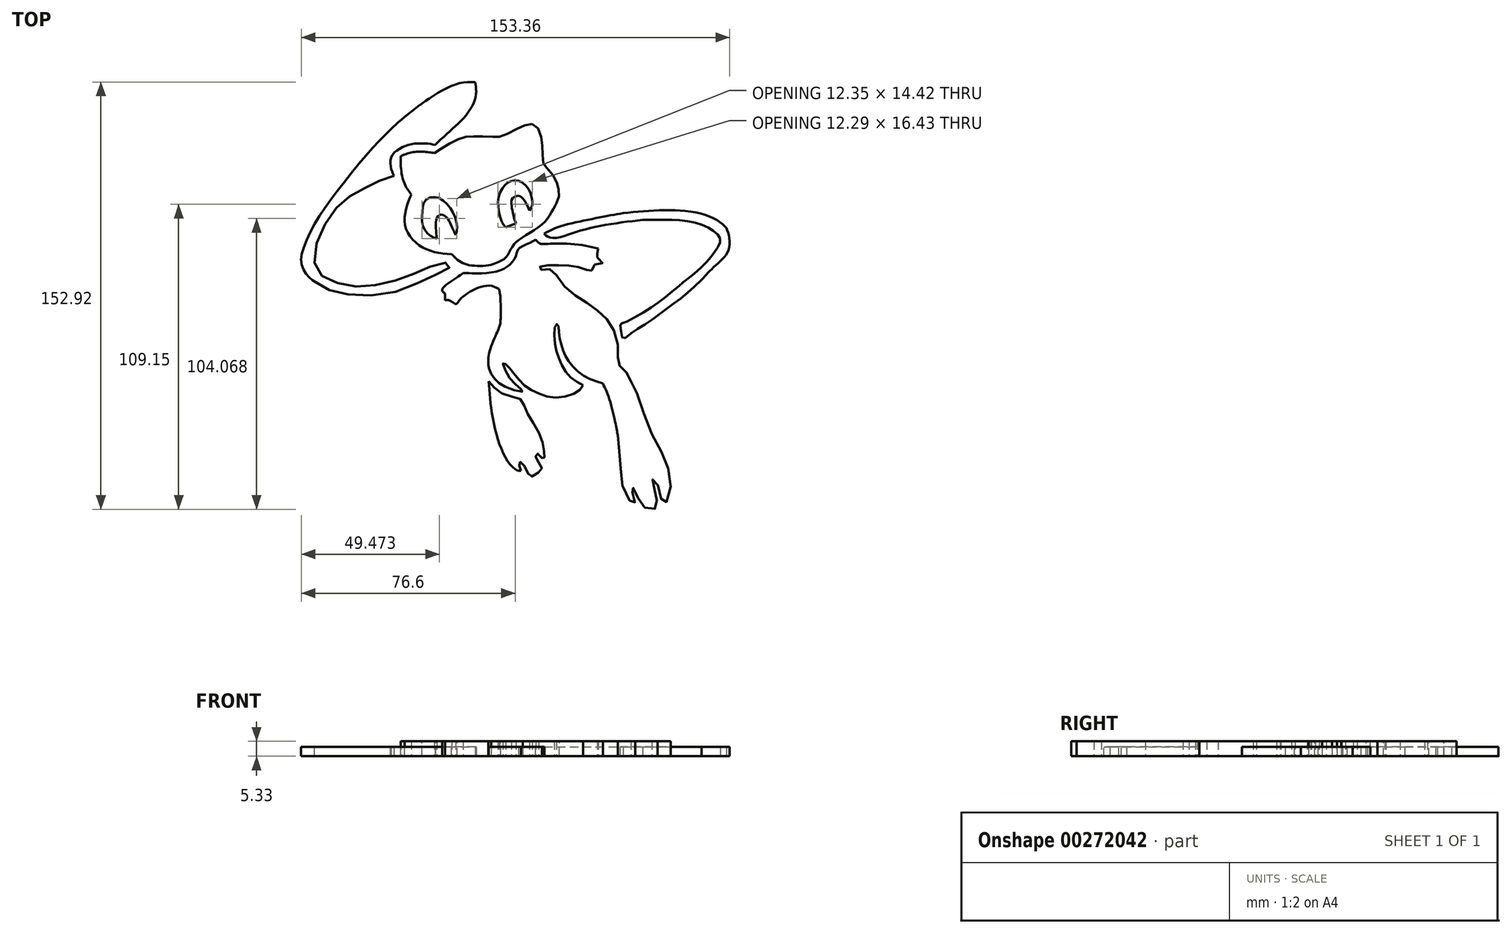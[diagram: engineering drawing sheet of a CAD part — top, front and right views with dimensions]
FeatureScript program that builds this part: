
annotation { "Feature Type Name" : "Feature", "Feature Type Description" : "" }
export const myFeature = defineFeature(function(context is Context, id is Id, definition is map)
    precondition{}
    {
        {
            var Q0;
            Q0=qCreatedBy(makeId("Top.planeOp"),FACE);
            var sketch = newSketch(context, id + "F0", { "sketchPlane" : qUnion([Q0])});
            skFitSpline(sketch, "E0", {"points": [v(-36.88, 36.08) * mm, v(-38.4, 38.25) * mm, v(-40.15, 42.6) * mm, v(-40.65, 48.33) * mm, v(-40.58, 49.85) * mm], "startDerivative": vector(-6.94, 9.09) * mm, "endDerivative": vector(0.6, 7.48) * mm});
            skFitSpline(sketch, "E1", {"points": [v(-40.58, 49.85) * mm, v(-38.04, 50.8) * mm, v(-34.93, 51.37) * mm, v(-31.38, 51.3) * mm, v(-28.55, 50.87) * mm], "startDerivative": vector(10.5, 4.31) * mm, "endDerivative": vector(11.28, -2.04) * mm});
            skFitSpline(sketch, "E2", {"points": [v(-28.55, 50.87) * mm, v(-24.87, 53.3) * mm, v(-19.99, 55.88) * mm, v(-16.36, 56.8) * mm, v(-12.2, 56.87) * mm, v(-6.98, 56.74) * mm, v(-4.41, 57) * mm, v(1, 59.57) * mm, v(4.83, 61.1) * mm, v(7.67, 60.76) * mm, v(9.65, 56.27) * mm, v(10.11, 52.11) * mm, v(10.44, 47.3) * mm, v(11.57, 45.71) * mm, v(14.54, 41.82) * mm, v(15.6, 38.91) * mm, v(16.05, 35.8) * mm, v(15.13, 32.97) * mm], "startDerivative": vector(55.8, 38.5) * mm, "endDerivative": vector(-24.9, -54.1) * mm});
            skFitSpline(sketch, "E3", {"points": [v(15.13, 32.97) * mm, v(13.23, 29.5) * mm, v(9.9, 25.32) * mm, v(3.54, 21.13) * mm, v(0, 18.38) * mm, v(-1.7, 15.62) * mm, v(-3.4, 13.15) * mm, v(-5.2, 12.2) * mm], "startDerivative": vector(-12.69, -24.26) * mm, "endDerivative": vector(-18.67, -6.95) * mm});
            skFitSpline(sketch, "E4", {"points": [v(-5.2, 12.2) * mm, v(-8.38, 10.92) * mm, v(-15.27, 10.68) * mm, v(-19.62, 12.2) * mm, v(-22.36, 14.64) * mm], "startDerivative": vector(-12.64, -6.7) * mm, "endDerivative": vector(-11.41, 11.76) * mm});
            skFitSpline(sketch, "E5", {"points": [v(-22.36, 14.64) * mm, v(-29.1, 15.62) * mm, v(-34.66, 18.38) * mm, v(-38.53, 23.3) * mm, v(-39.1, 28.91) * mm, v(-37.75, 33.9) * mm, v(-36.88, 36.08) * mm], "startDerivative": vector(-36.55, 3.17) * mm, "endDerivative": vector(7.3, 17.53) * mm});
            skFitSpline(sketch, "E6", {"points": [v(-27.74, 20.26) * mm, v(-28, 23.55) * mm, v(-27.97, 26.8) * mm, v(-27.14, 28.47) * mm, v(-25.9, 28.88) * mm, v(-24.15, 27.82) * mm, v(-22.83, 25.7) * mm, v(-21.65, 22.95) * mm, v(-20.94, 21.55) * mm], "startDerivative": vector(-1.85, 21.58) * mm, "endDerivative": vector(6.7, -12.08) * mm});
            skFitSpline(sketch, "E7", {"points": [v(-20.94, 21.55) * mm, v(-20.44, 24.42) * mm, v(-21.43, 28.58) * mm, v(-23.73, 32.29) * mm, v(-27.18, 34.9) * mm, v(-30.4, 34.9) * mm, v(-32.4, 32.97) * mm, v(-32.96, 29.53) * mm, v(-32.93, 25.74) * mm, v(-31.6, 22.72) * mm, v(-29.48, 20.98) * mm, v(-27.74, 20.26) * mm], "startDerivative": vector(8.86, 31.93) * mm, "endDerivative": vector(24.92, -8.61) * mm});
            skLineSegment(sketch, "E8", {"start": v(0.64, 25.77) * mm, "end": v(-3.1, 24.33) * mm});
            skFitSpline(sketch, "E9", {"points": [v(-3.1, 24.33) * mm, v(-4.7, 26.86) * mm, v(-5.73, 31.34) * mm, v(-5.33, 36.17) * mm, v(-3.1, 39.67) * mm, v(-0.97, 40.88) * mm, v(1.96, 40.82) * mm, v(4.95, 38.23) * mm, v(6.27, 34.79) * mm, v(6.39, 32.09) * mm, v(5.4, 30.37) * mm], "startDerivative": vector(-18.53, 24.2) * mm, "endDerivative": vector(-15.72, -20.8) * mm});
            skFitSpline(sketch, "E10", {"points": [v(5.4, 30.37) * mm, v(4.03, 33.3) * mm, v(2.36, 35.3) * mm, v(1.16, 35.6) * mm, v(-0.68, 34.67) * mm, v(-1.02, 32.66) * mm, v(-0.68, 30.37) * mm, v(0, 27.55) * mm, v(0.64, 25.77) * mm], "startDerivative": vector(-8.23, 19.96) * mm, "endDerivative": vector(5.68, -14.34) * mm});
            skFitSpline(sketch, "E11", {"points": [v(-28.3, 53.85) * mm, v(-22.62, 59.17) * mm, v(-17.41, 64.25) * mm, v(-14.15, 69.88) * mm, v(-13.66, 73.45) * mm, v(-13.97, 76.31) * mm], "startDerivative": vector(23.72, 22.62) * mm, "endDerivative": vector(-2.81, 19.35) * mm});
            skFitSpline(sketch, "E12", {"points": [v(-13.97, 76.31) * mm, v(-19.11, 76) * mm, v(-25.25, 73.58) * mm, v(-32.16, 69.26) * mm, v(-37.13, 65.53) * mm, v(-41.53, 61.88) * mm, v(-44.08, 59.5) * mm], "startDerivative": vector(-32.41, 0.3) * mm, "endDerivative": vector(-18.17, -17.44) * mm});
            skFitSpline(sketch, "E13", {"points": [v(-44.08, 59.5) * mm, v(-51.8, 51.48) * mm, v(-63.2, 37.48) * mm, v(-71.34, 25.77) * mm, v(-75.54, 16.64) * mm, v(-76.22, 11.77) * mm, v(-74.95, 8.38) * mm, v(-73.1, 6.15) * mm, v(-70.98, 4.61) * mm], "startDerivative": vector(-48.4, -47.85) * mm, "endDerivative": vector(29.7, -19.4) * mm});
            skFitSpline(sketch, "E14", {"points": [v(-70.98, 4.61) * mm, v(-65.73, 1.76) * mm, v(-56.11, 0) * mm, v(-41.53, 1.5) * mm, v(-30.47, 6.38) * mm, v(-23.8, 9.45) * mm, v(-22.65, 11) * mm, v(-25.86, 11.63) * mm, v(-32.16, 9.32) * mm, v(-40.09, 6.12) * mm, v(-50.09, 3.56) * mm, v(-58.94, 3.43) * mm, v(-66.88, 5.86) * mm, v(-70.98, 9.58) * mm, v(-70.98, 17.91) * mm, v(-66.24, 27.79) * mm, v(-60.86, 34.07) * mm, v(-54.7, 37.79) * mm, v(-48.55, 40.86) * mm, v(-43.04, 42.79) * mm], "startDerivative": vector(103.96, -66.84) * mm, "endDerivative": vector(119.1, 36.89) * mm});
            skFitSpline(sketch, "E15", {"points": [v(-43.04, 42.79) * mm, v(-44.08, 45.32) * mm, v(-44.08, 49.34) * mm, v(-41, 52.5) * mm, v(-36.55, 54.15) * mm, v(-31.3, 54.3) * mm, v(-28.3, 53.85) * mm], "startDerivative": vector(-8.33, 16.7) * mm, "endDerivative": vector(18.9, -3.53) * mm});
            skFitSpline(sketch, "E16", {"points": [v(7.73, 19.96) * mm, v(4.7, 18.38) * mm, v(1.47, 16.59) * mm, v(0.64, 14.22) * mm, v(-1.21, 11.37) * mm, v(-4.34, 9.18) * mm, v(-10.33, 7.93) * mm, v(-15.9, 7.9) * mm, v(-18.3, 8) * mm], "startDerivative": vector(-23.75, -13.65) * mm, "endDerivative": vector(-21.58, 1.02) * mm});
            skFitSpline(sketch, "E17", {"points": [v(-18.3, 8) * mm, v(-21.48, 5.79) * mm, v(-25.73, 2.22) * mm, v(-25.51, 1.24) * mm, v(-24.96, 0.69) * mm, v(-24.75, -0.76) * mm, v(-24.75, -1.78) * mm], "startDerivative": vector(-11.77, -8.3) * mm, "endDerivative": vector(-0.07, -7.72) * mm});
            skFitSpline(sketch, "E18", {"points": [v(-24.75, -1.78) * mm, v(-23.18, -1.78) * mm, v(-20.94, -3.12) * mm, v(-19.7, -1.78) * mm, v(-15.31, 1.57) * mm, v(-11.82, 3.08) * mm, v(-8.28, 3.4) * mm, v(-5.41, 2.2) * mm], "startDerivative": vector(14.29, 3.8) * mm, "endDerivative": vector(18.83, -10.57) * mm});
            skFitSpline(sketch, "E19", {"points": [v(-5.41, -11.46) * mm, v(-6.46, -13.9) * mm, v(-8.5, -18.88) * mm, v(-9.27, -22.77) * mm, v(-9.19, -25.46) * mm, v(-8.23, -28.1) * mm], "startDerivative": vector(-5.21, -12.45) * mm, "endDerivative": vector(6.45, -14.59) * mm});
            skFitSpline(sketch, "E20", {"points": [v(-5.41, -11.46) * mm, v(-5.02, -10.14) * mm, v(-4.86, -5.9) * mm, v(-5.02, -0.37) * mm, v(-5.41, 2.2) * mm], "startDerivative": vector(2.76, 6.94) * mm, "endDerivative": vector(-2.02, 10.26) * mm});
            skFitSpline(sketch, "E21", {"points": [v(-8.23, -28.1) * mm, v(-6.3, -30.62) * mm, v(-2.7, -32.95) * mm, v(3.02, -34.4) * mm, v(1.33, -32.7) * mm, v(-2.6, -28.1) * mm, v(-3.98, -24.1) * mm, v(-2.53, -25.15) * mm, v(0, -28.1) * mm, v(3.82, -32.39) * mm, v(9.45, -35.44) * mm, v(15.89, -36.57) * mm, v(22.56, -34.56) * mm, v(24.65, -32.14) * mm], "startDerivative": vector(28.07, -40.83) * mm, "endDerivative": vector(24.08, 39.06) * mm});
            skFitSpline(sketch, "E22", {"points": [v(24.65, -32.14) * mm, v(19.46, -28.61) * mm, v(16.04, -22.68) * mm, v(14.52, -16.3) * mm, v(14.9, -10.44) * mm, v(15.66, -10.59) * mm, v(15.96, -13.48) * mm, v(17.1, -18.5) * mm, v(18.55, -22.07) * mm, v(21.74, -26.25) * mm, v(26.3, -29.6) * mm, v(31.7, -31.5) * mm], "startDerivative": vector(-53.5, 28.4) * mm, "endDerivative": vector(55.72, -15.9) * mm});
            skFitSpline(sketch, "E23", {"points": [v(31.7, -31.5) * mm, v(33.83, -36.52) * mm, v(35.88, -44.2) * mm, v(36.72, -48.3) * mm, v(37.03, -50.06) * mm], "startDerivative": vector(8, -16.8) * mm, "endDerivative": vector(1.73, -10.31) * mm});
            skFitSpline(sketch, "E24", {"points": [v(37.03, -50.06) * mm, v(37.67, -56.88) * mm, v(38.28, -65.1) * mm, v(40.12, -71.84) * mm, v(43.18, -74.9) * mm, v(43.1, -73.5) * mm, v(42.4, -70.97) * mm, v(41.78, -68.6) * mm, v(42.74, -69.04) * mm, v(44.05, -72.02) * mm, v(46.24, -75.6) * mm, v(48.43, -76.56) * mm, v(50.96, -76.04) * mm, v(51.14, -73.77) * mm, v(50.44, -70) * mm, v(49.3, -67.03) * mm, v(49.65, -65.8) * mm, v(50.96, -67.03) * mm, v(52.28, -70.88) * mm, v(53.41, -74.73) * mm, v(55.25, -72.45) * mm, v(55.69, -64.58) * mm, v(52.89, -56.53) * mm, v(48, -46.82) * mm, v(43.88, -35.1) * mm, v(41.78, -30.72) * mm], "startDerivative": vector(13.24, -128.19) * mm, "endDerivative": vector(-47.37, 85.69) * mm});
            skFitSpline(sketch, "E25", {"points": [v(41.78, -30.72) * mm, v(39.73, -27.08) * mm, v(37.25, -24.41) * mm, v(37.25, -19.83) * mm, v(34.98, -11.16) * mm, v(30.4, -6) * mm, v(23.99, -1.41) * mm, v(17.4, 3.84) * mm, v(13.4, 9.09) * mm, v(11.07, 9.25) * mm, v(8.74, 9.34) * mm, v(9.57, 10.42) * mm, v(12.82, 10.75) * mm, v(17.74, 10.75) * mm, v(21.82, 10.34) * mm, v(25.32, 9.42) * mm, v(27.49, 8.42) * mm, v(27.82, 9.75) * mm, v(29.73, 11.34) * mm, v(31.7, 11.67) * mm, v(30.07, 13.17) * mm], "startDerivative": vector(-32.27, 75.78) * mm, "endDerivative": vector(-69.54, 49.62) * mm});
            skFitSpline(sketch, "E26", {"points": [v(30.07, 13.17) * mm, v(29.68, 13.9) * mm, v(30.07, 16.7) * mm], "startDerivative": vector(-1.4, 1.7) * mm, "endDerivative": vector(1.15, 5.02) * mm});
            skFitSpline(sketch, "E27", {"points": [v(30.07, 16.7) * mm, v(22.73, 18.2) * mm, v(13.95, 18.48) * mm, v(10.79, 18.39) * mm, v(9.05, 18.57) * mm, v(7.73, 19.96) * mm], "startDerivative": vector(-25.6, 6.72) * mm, "endDerivative": vector(-8.87, 12.5) * mm});
            skFitSpline(sketch, "E28", {"points": [v(2.36, -62.8) * mm, v(0.76, -62.5) * mm, v(-2.57, -59) * mm, v(-6.3, -50.06) * mm, v(-8.47, -38.73) * mm, v(-9.1, -30.72) * mm], "startDerivative": vector(-15.3, 0.2) * mm, "endDerivative": vector(-2, 34.43) * mm});
            skFitSpline(sketch, "E29", {"points": [v(-9.1, -30.72) * mm, v(-6.83, -33.36) * mm, v(-2.86, -35.76) * mm, v(1.7, -36.87) * mm, v(3.27, -38.68) * mm, v(4.67, -42.12) * mm, v(7.73, -47.26) * mm, v(9.98, -52.26) * mm, v(10.68, -55.72) * mm, v(10.74, -57.77) * mm, v(10.68, -58.76) * mm, v(9.52, -57.7) * mm, v(8.4, -56.66) * mm, v(7.73, -56.9) * mm, v(7.73, -58) * mm, v(9, -60.22) * mm, v(9.87, -61.8) * mm, v(9.4, -62.79) * mm, v(7, -64.42) * mm, v(5.66, -64.95) * mm, v(4.55, -62.96) * mm, v(3.15, -60.4) * mm, v(2.1, -59.64) * mm, v(1.63, -60.1) * mm, v(1.87, -61.39) * mm, v(2.36, -62.8) * mm], "startDerivative": vector(41.4, -54) * mm, "endDerivative": vector(14.87, -42.66) * mm});
            skFitSpline(sketch, "E30", {"points": [v(10.72, 22.02) * mm, v(15.3, 24.28) * mm, v(23.56, 26.44) * mm, v(32.84, 28.33) * mm, v(38.94, 29.4) * mm], "startDerivative": vector(20, 11.39) * mm, "endDerivative": vector(24.9, 4.23) * mm});
            skFitSpline(sketch, "E31", {"points": [v(10.72, 22.02) * mm, v(12.02, 21) * mm, v(14.93, 20.56) * mm, v(20, 22.02) * mm, v(27.23, 24.07) * mm, v(36.57, 25.8) * mm, v(46, 27.03) * mm], "startDerivative": vector(12.39, -12.48) * mm, "endDerivative": vector(43.26, 5.28) * mm});
            skFitSpline(sketch, "E32", {"points": [v(46, 27.03) * mm, v(54.46, 27.03) * mm, v(64.58, 26.06) * mm, v(71.34, 23.07) * mm, v(73.7, 20) * mm, v(72.38, 16.45) * mm, v(68.06, 11.1) * mm, v(62.98, 6.64) * mm, v(59.01, 3.36) * mm], "startDerivative": vector(56.72, 0.57) * mm, "endDerivative": vector(-34.14, -28.32) * mm});
            skFitSpline(sketch, "E33", {"points": [v(38.94, 29.4) * mm, v(48.57, 30.24) * mm, v(58.73, 30.38) * mm, v(68.13, 28.85) * mm, v(73.84, 26.06) * mm, v(75.93, 24.11) * mm], "startDerivative": vector(41.77, 4.1) * mm, "endDerivative": vector(14.3, -15.48) * mm});
            skFitSpline(sketch, "E34", {"points": [v(59.01, 3.36) * mm, v(52.8, -1.66) * mm, v(46, -6.28) * mm, v(38.94, -9.92) * mm, v(37.93, -10.28) * mm, v(38.17, -12.05) * mm, v(38.94, -15.45) * mm, v(41.63, -13.75) * mm, v(47.58, -9.92) * mm, v(54.08, -5.19) * mm, v(60.39, -0.45) * mm, v(67.07, 5.5) * mm], "startDerivative": vector(-56.72, -47.28) * mm, "endDerivative": vector(57.6, 53.68) * mm});
            skFitSpline(sketch, "E35", {"points": [v(67.07, 5.5) * mm, v(71.5, 10.15) * mm, v(76.76, 16.45) * mm, v(75.93, 24.11) * mm], "startDerivative": vector(12.97, 14.55) * mm, "endDerivative": vector(-7.34, 15.71) * mm});
            skSolve(sketch);
        }
        {
            var Q0;
            Q0=makeQuery(id+"F0.imprint","IMPRINT",FACE,{"disambiguationData":[TD([[makeQuery(id+"F0.imprint","IMPRINT",EDGE,{"derivedFrom":sQuery(id+"F0.wireOp",EDGE,"E0")}),-1.0]])]});
            var Q1;
            Q1=makeQuery(id+"F0.imprint","IMPRINT",FACE,{"disambiguationData":[TD([[makeQuery(id+"F0.imprint","IMPRINT",EDGE,{"derivedFrom":sQuery(id+"F0.wireOp",EDGE,"E16")}),1.0]])]});
            extrude(context, id + "F1", {"entities" : qUnion([Q0, Q1]), "depth" : 5.33 * mm});
        }
        {
            var Q0;
            Q0=makeQuery(id+"F0.imprint","IMPRINT",FACE,{"disambiguationData":[TD([[makeQuery(id+"F0.imprint","IMPRINT",EDGE,{"derivedFrom":sQuery(id+"F0.wireOp",EDGE,"E11")}),1.0]])]});
            var Q1;
            Q1=makeQuery(id+"F0.imprint","IMPRINT",FACE,{"disambiguationData":[TD([[makeQuery(id+"F0.imprint","IMPRINT",EDGE,{"derivedFrom":sQuery(id+"F0.wireOp",EDGE,"E28")}),-1.0]])]});
            var Q2;
            Q2=makeQuery(id+"F0.imprint","IMPRINT",FACE,{"disambiguationData":[TD([[makeQuery(id+"F0.imprint","IMPRINT",EDGE,{"derivedFrom":sQuery(id+"F0.wireOp",EDGE,"E30")}),-1.0]])]});
            extrude(context, id + "F2", {"entities" : qUnion([Q0, Q1, Q2]), "depth" : 3.3 * mm});
        }
    });
